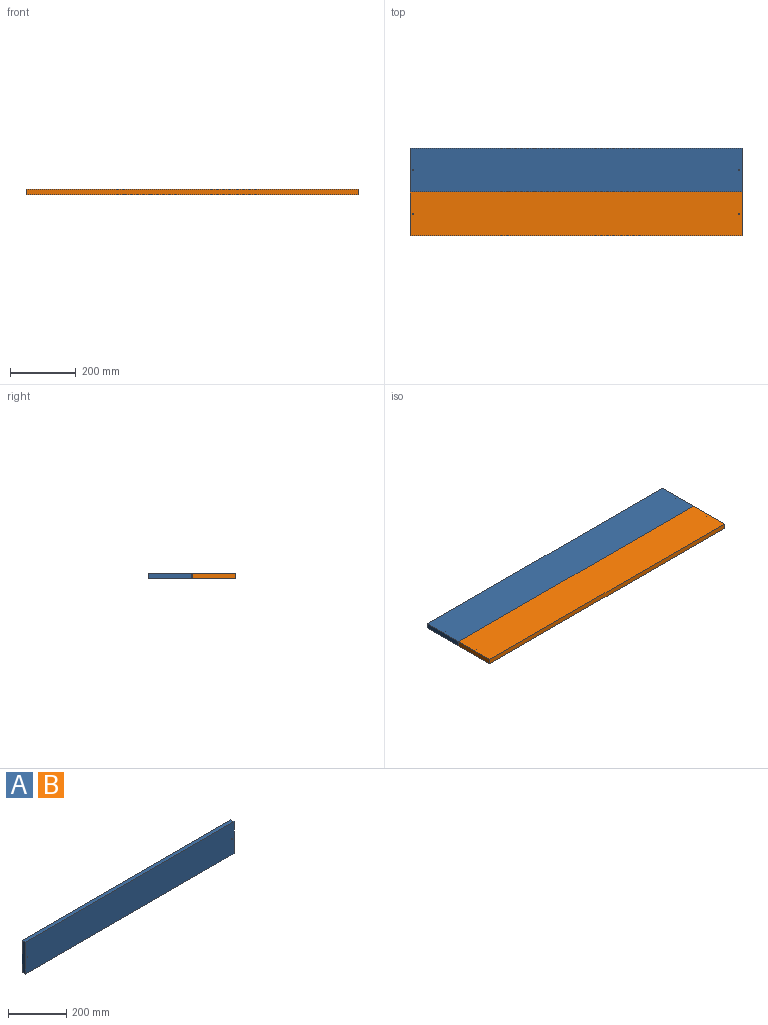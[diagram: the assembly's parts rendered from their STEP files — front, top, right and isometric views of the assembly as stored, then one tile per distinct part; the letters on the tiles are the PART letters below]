
ASSEMBLY  parts=2 mates=1
PART A: 8 faces, bbox 1009.7x15.9x133.4 mm
  f0: plane 1009.65x15.88mm, normal (0,0,1), area 16028.2mm2, adj f1,f3,f4,f5
  f1: plane 133.35x15.88mm, normal (-1,0,0), area 2116.9mm2, adj f0,f2,f4,f5
  f2: plane 1009.65x15.88mm, normal (0,0,-1), area 16028.2mm2, adj f1,f3,f4,f5
  f3: plane 133.35x15.88mm, normal (1,0,0), area 2116.9mm2, adj f0,f2,f4,f5
  f4: plane 1009.65x133.35mm, normal (0,-1,0), area 134632.9mm2, adj f0,f1,f2,f3,f6,f7
  f5: plane 1009.65x133.35mm, normal (0,1,0), area 134632.9mm2, adj f0,f1,f2,f3,f6,f7
  f6: cylinder r=0.79mm len=15.88mm, axis (0,1,0), area 79.2mm2, adj f4,f5
  f7: cylinder r=0.79mm len=15.88mm, axis (0,1,0), area 79.2mm2, adj f4,f5
PART B: same geometry as A
PLACE A rot(axis=(-1,0,0),90deg) t=(-15.42,0.21,-11.1)mm
PLACE B rot(axis=(-1,0,0),90deg) t=(-15.42,-133.14,-11.1)mm
MATE fastened A.f2 <-> B.f0  axis (0,-1,0) through (-15.42,0.21,-3.16)mm
